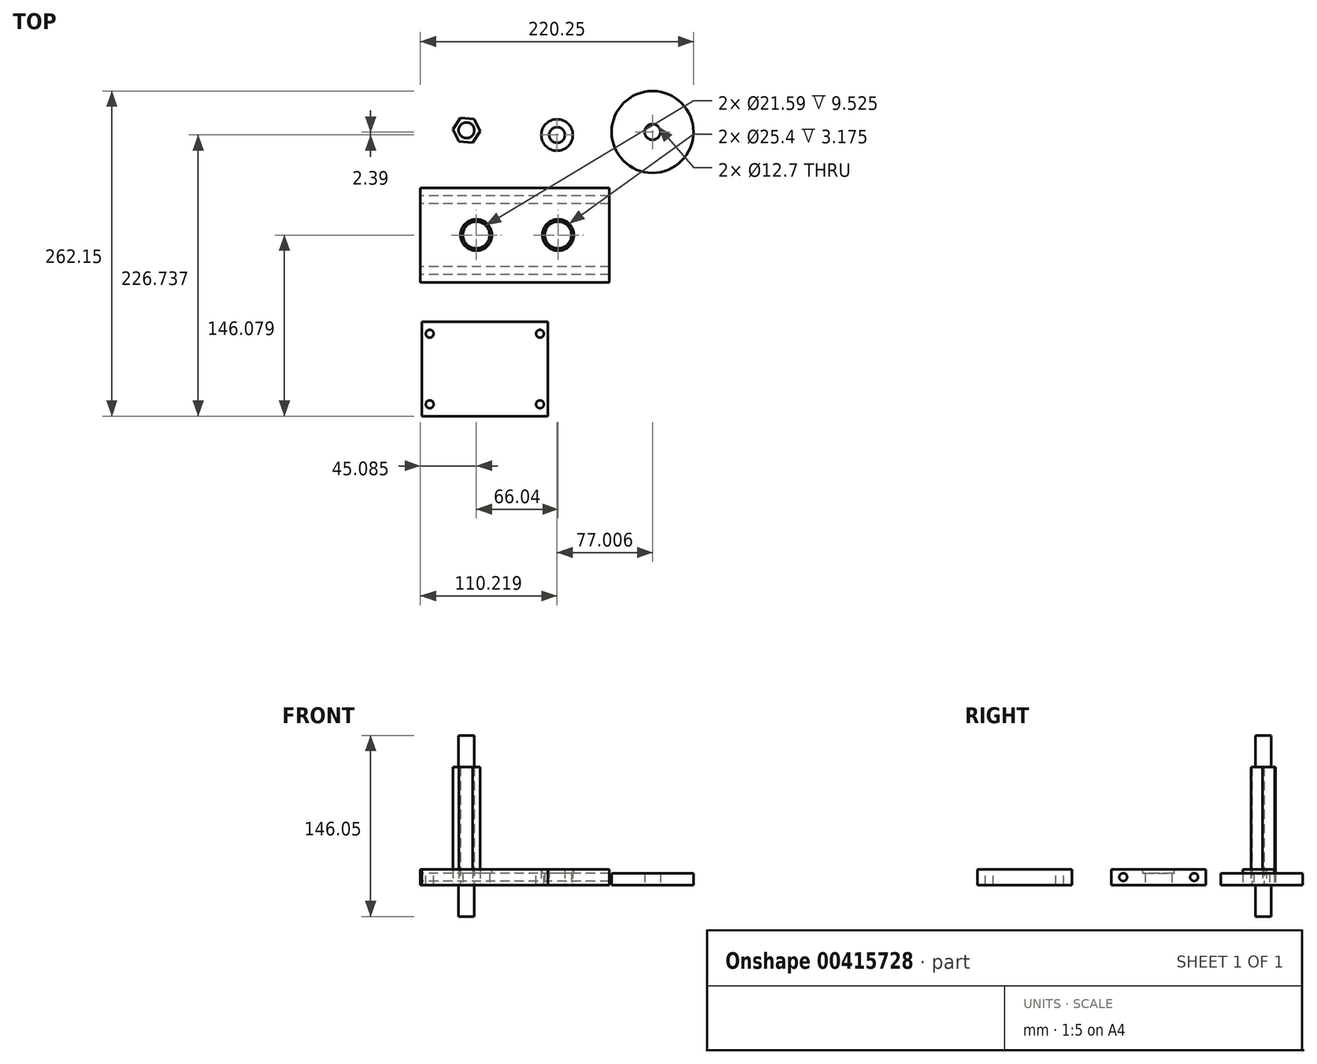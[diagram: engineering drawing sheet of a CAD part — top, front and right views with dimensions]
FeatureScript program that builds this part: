
annotation { "Feature Type Name" : "Feature", "Feature Type Description" : "" }
export const myFeature = defineFeature(function(context is Context, id is Id, definition is map)
    precondition{}
    {
        {
            var Q0;
            Q0=qCreatedBy(makeId("Top.planeOp"),FACE);
            var sketch = newSketch(context, id + "F0", { "sketchPlane" : qUnion([Q0])});
            skCircle(sketch, "E0.cCircle", {"center": v(-38.25, 33.87) * mm, "radius": 9.53 * mm, "construction": true});
            skLineSegment(sketch, "E0.0", {"start": v(-27.28, 33.16) * mm, "end": v(-33.38, 24.01) * mm});
            skLineSegment(sketch, "E0.1", {"start": v(-33.38, 24.01) * mm, "end": v(-44.35, 24.72) * mm});
            skLineSegment(sketch, "E0.2", {"start": v(-44.35, 24.72) * mm, "end": v(-49.23, 34.58) * mm});
            skLineSegment(sketch, "E0.3", {"start": v(-49.23, 34.58) * mm, "end": v(-43.13, 43.73) * mm});
            skLineSegment(sketch, "E0.4", {"start": v(-43.13, 43.73) * mm, "end": v(-32.15, 43.02) * mm});
            skLineSegment(sketch, "E0.5", {"start": v(-32.15, 43.02) * mm, "end": v(-27.28, 33.16) * mm});
            skPoint(sketch, "E0.0.midPoint", {"position": v(-30.33, 28.59) * mm});
            skSolve(sketch);
        }
        {
            var Q0;
            Q0 = qSketchRegion(id + "F0", true);
            extrude(context, id + "F1", {"entities" : qUnion([Q0]), "depth" : 95.25 * mm});
        }
        {
            var Q0;
            Q0=makeQuery(id+"F1.opExtrude","CAP_FACE",FACE,{"disambiguationData":[OSD([sQuery(id+"F0.wireOp",EDGE,"E0.0"),sQuery(id+"F0.wireOp",EDGE,"E0.1"),sQuery(id+"F0.wireOp",EDGE,"E0.2"),sQuery(id+"F0.wireOp",EDGE,"E0.3"),sQuery(id+"F0.wireOp",EDGE,"E0.4"),sQuery(id+"F0.wireOp",EDGE,"E0.5")])],"isStart":false});
            var sketch = newSketch(context, id + "F2", { "sketchPlane" : qUnion([Q0])});
            skLineSegment(sketch, "E1", {"start": v(-43.13, 43.73) * mm, "end": v(-33.38, 24.01) * mm, "construction": true});
            skCircle(sketch, "E2", {"center": v(-38.25, 33.87) * mm, "radius": 6.35 * mm});
            skSolve(sketch);
        }
        {
            var Q0;
            Q0 = qSketchRegion(id + "F2", true);
            extrude(context, id + "F3", {"entities" : qUnion([Q0]), "operationType" : NewBodyOperationType.ADD, "depth" : 25.4 * mm});
        }
        {
            var Q0;
            Q0=makeQuery(id+"F1.opExtrude","CAP_FACE",FACE,{"disambiguationData":[OSD([sQuery(id+"F0.wireOp",EDGE,"E0.0"),sQuery(id+"F0.wireOp",EDGE,"E0.1"),sQuery(id+"F0.wireOp",EDGE,"E0.2"),sQuery(id+"F0.wireOp",EDGE,"E0.3"),sQuery(id+"F0.wireOp",EDGE,"E0.4"),sQuery(id+"F0.wireOp",EDGE,"E0.5")])],"isStart":true});
            var sketch = newSketch(context, id + "F4", { "sketchPlane" : qUnion([Q0])});
            skLineSegment(sketch, "E3", {"start": v(-43.13, -43.73) * mm, "end": v(-33.38, -24.01) * mm, "construction": true});
            skCircle(sketch, "E4", {"center": v(-38.25, -33.87) * mm, "radius": 6.35 * mm});
            skSolve(sketch);
        }
        {
            var Q0;
            Q0 = qSketchRegion(id + "F4", true);
            extrude(context, id + "F5", {"entities" : qUnion([Q0]), "operationType" : NewBodyOperationType.ADD, "depth" : 25.4 * mm});
        }
        {
            var Q0;
            Q0=qCreatedBy(makeId("Top.planeOp"),FACE);
            var sketch = newSketch(context, id + "F6", { "sketchPlane" : qUnion([Q0])});
            skCircle(sketch, "E5", {"center": v(34.75, 30.08) * mm, "radius": 6.35 * mm});
            skCircle(sketch, "E6", {"center": v(34.75, 30.08) * mm, "radius": 12.7 * mm});
            skSolve(sketch);
        }
        {
            var Q0;
            Q0 = qSketchRegion(id + "F6", true);
            extrude(context, id + "F7", {"entities" : qUnion([Q0]), "depth" : 12.7 * mm});
        }
        {
            var Q0;
            Q0=qCreatedBy(makeId("Top.planeOp"),FACE);
            var sketch = newSketch(context, id + "F8", { "sketchPlane" : qUnion([Q0])});
            skLineSegment(sketch, "E7.bottom", {"start": v(-75.47, -12.48) * mm, "end": v(76.93, -12.48) * mm});
            skLineSegment(sketch, "E7.top", {"start": v(-75.47, -88.68) * mm, "end": v(76.93, -88.68) * mm});
            skLineSegment(sketch, "E7.left", {"start": v(-75.47, -12.48) * mm, "end": v(-75.47, -88.68) * mm});
            skLineSegment(sketch, "E7.right", {"start": v(76.93, -12.48) * mm, "end": v(76.93, -88.68) * mm});
            skCircle(sketch, "E8", {"center": v(-30.39, -50.58) * mm, "radius": 10.8 * mm});
            skCircle(sketch, "E9", {"center": v(35.65, -50.58) * mm, "radius": 10.8 * mm});
            skLineSegment(sketch, "E10", {"start": v(-75.47, -50.58) * mm, "end": v(76.93, -50.58) * mm, "construction": true});
            skSolve(sketch);
        }
        {
            var Q0;
            Q0 = qSketchRegion(id + "F8", true);
            extrude(context, id + "F9", {"entities" : qUnion([Q0]), "depth" : 12.7 * mm});
        }
        {
            var Q0;
            Q0=makeQuery(id+"F9.opExtrude","CAP_FACE",FACE,{"disambiguationData":[OSD([sQuery(id+"F8.wireOp",EDGE,"E7.bottom"),sQuery(id+"F8.wireOp",EDGE,"E7.top"),sQuery(id+"F8.wireOp",EDGE,"E7.left"),sQuery(id+"F8.wireOp",EDGE,"E7.right"),sQuery(id+"F8.wireOp",EDGE,"E8"),sQuery(id+"F8.wireOp",EDGE,"E9")])],"isStart":false});
            var sketch = newSketch(context, id + "F10", { "sketchPlane" : qUnion([Q0])});
            skCircle(sketch, "E11", {"center": v(-30.39, -50.58) * mm, "radius": 12.7 * mm});
            skCircle(sketch, "E12", {"center": v(35.65, -50.58) * mm, "radius": 12.7 * mm});
            skSolve(sketch);
        }
        {
            var Q0;
            Q0 = qSketchRegion(id + "F10", true);
            extrude(context, id + "F11", {"entities" : qUnion([Q0]), "operationType" : NewBodyOperationType.REMOVE, "oppositeDirection" : true, "depth" : 3.17 * mm});
        }
        {
            var Q0;
            Q0=qCreatedBy(makeId("Top.planeOp"),FACE);
            var sketch = newSketch(context, id + "F12", { "sketchPlane" : qUnion([Q0])});
            skLineSegment(sketch, "E13.bottom", {"start": v(-74.27, -120.46) * mm, "end": v(27.33, -120.46) * mm});
            skLineSegment(sketch, "E13.top", {"start": v(-74.27, -196.66) * mm, "end": v(27.33, -196.66) * mm});
            skLineSegment(sketch, "E13.left", {"start": v(-74.27, -120.46) * mm, "end": v(-74.27, -196.66) * mm});
            skLineSegment(sketch, "E13.right", {"start": v(27.33, -120.46) * mm, "end": v(27.33, -196.66) * mm});
            skSolve(sketch);
        }
        {
            var Q0;
            Q0 = qSketchRegion(id + "F12", true);
            extrude(context, id + "F13", {"entities" : qUnion([Q0]), "depth" : 12.7 * mm});
        }
        {
            var Q0;
            Q0=makeQuery(id+"F9.opExtrude","SWEPT_FACE",FACE,{"disambiguationData":[OSD([sQuery(id+"F8.wireOp",EDGE,"E7.left")])]});
            var sketch = newSketch(context, id + "F14", { "sketchPlane" : qUnion([Q0])});
            skCircle(sketch, "E14", {"center": v(22, 6.35) * mm, "radius": 3.18 * mm});
            skCircle(sketch, "E15", {"center": v(79.16, 6.35) * mm, "radius": 3.18 * mm});
            skSolve(sketch);
        }
        {
            var Q0;
            Q0 = qSketchRegion(id + "F14", true);
            extrude(context, id + "F15", {"entities" : qUnion([Q0]), "operationType" : NewBodyOperationType.REMOVE, "endBound" : BoundingType.THROUGH_ALL, "oppositeDirection" : true, "depth" : 25.4 * mm});
        }
        {
            var Q0;
            Q0=qCreatedBy(makeId("Top.planeOp"),FACE);
            var sketch = newSketch(context, id + "F16", { "sketchPlane" : qUnion([Q0])});
            skCircle(sketch, "E16", {"center": v(111.76, 32.47) * mm, "radius": 6.35 * mm});
            skCircle(sketch, "E17", {"center": v(111.76, 32.47) * mm, "radius": 33.02 * mm});
            skSolve(sketch);
        }
        {
            var Q0;
            Q0 = qSketchRegion(id + "F16", true);
            extrude(context, id + "F17", {"entities" : qUnion([Q0]), "depth" : 9.52 * mm});
        }
        {
            var Q0;
            Q0=makeQuery(id+"F13.opExtrude","CAP_FACE",FACE,{"disambiguationData":[OSD([sQuery(id+"F12.wireOp",EDGE,"E13.bottom"),sQuery(id+"F12.wireOp",EDGE,"E13.top"),sQuery(id+"F12.wireOp",EDGE,"E13.left"),sQuery(id+"F12.wireOp",EDGE,"E13.right")])],"isStart":false});
            var sketch = newSketch(context, id + "F18", { "sketchPlane" : qUnion([Q0])});
            skCircle(sketch, "E18", {"center": v(-67.92, -130.24) * mm, "radius": 3.18 * mm});
            skCircle(sketch, "E19", {"center": v(-67.92, -187.14) * mm, "radius": 3.18 * mm});
            skCircle(sketch, "E20", {"center": v(20.98, -130.24) * mm, "radius": 3.18 * mm});
            skCircle(sketch, "E21", {"center": v(20.98, -187.14) * mm, "radius": 3.18 * mm});
            skSolve(sketch);
        }
        {
            var Q0;
            Q0 = qSketchRegion(id + "F18", true);
            extrude(context, id + "F19", {"entities" : qUnion([Q0]), "operationType" : NewBodyOperationType.REMOVE, "endBound" : BoundingType.THROUGH_ALL, "oppositeDirection" : true, "depth" : 25.4 * mm});
        }
    });
